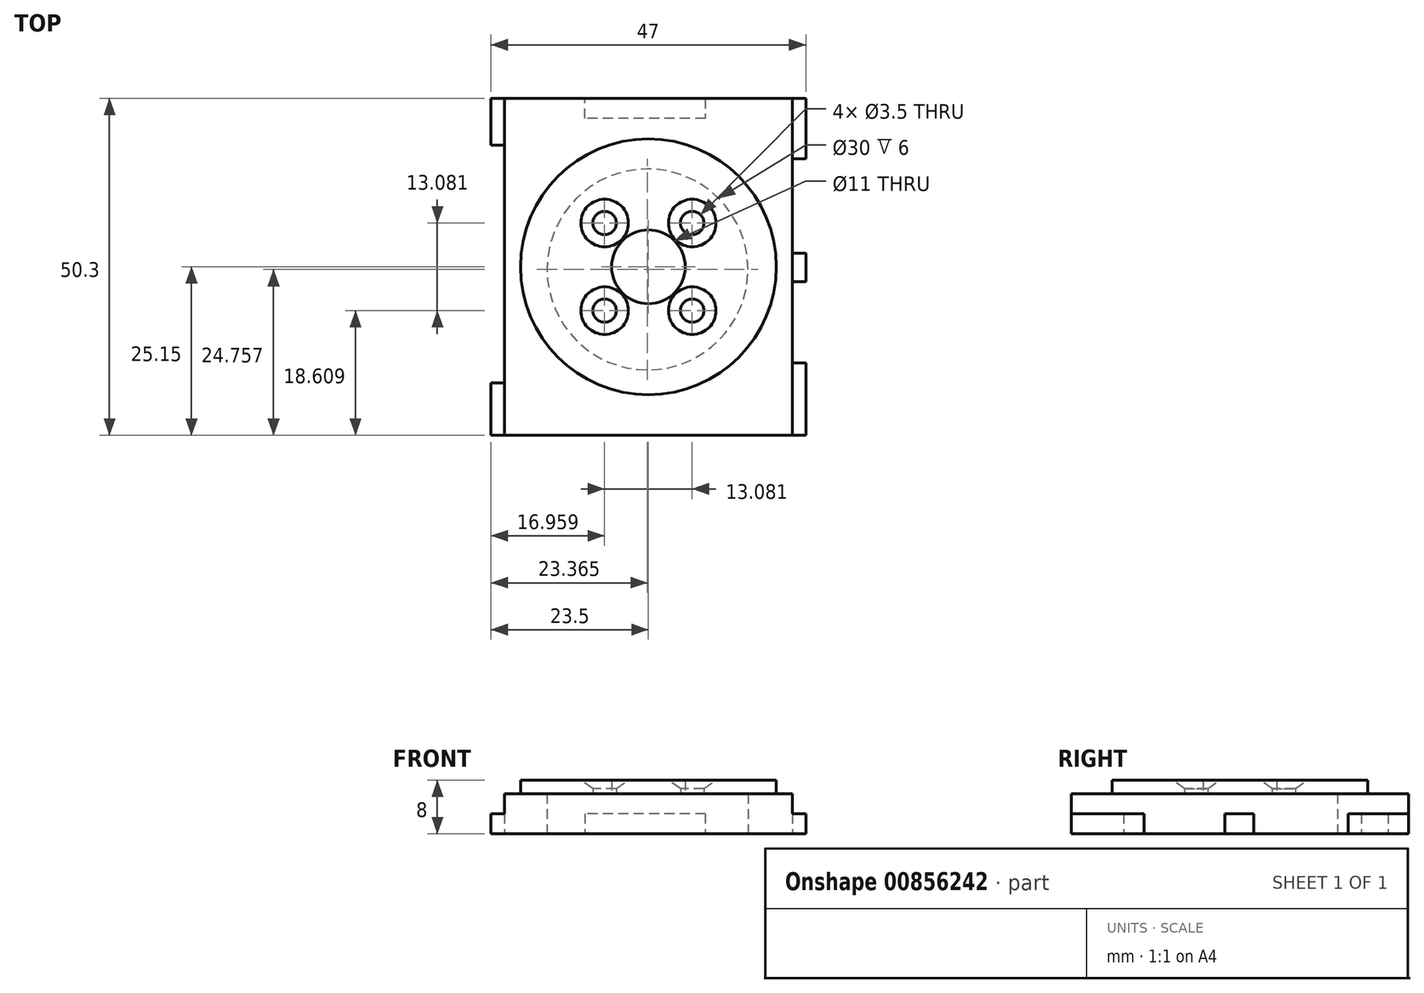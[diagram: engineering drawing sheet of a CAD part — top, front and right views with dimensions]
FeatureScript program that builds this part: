
annotation { "Feature Type Name" : "Feature", "Feature Type Description" : "" }
export const myFeature = defineFeature(function(context is Context, id is Id, definition is map)
    precondition{}
    {
        {
            var Q0;
            Q0=qCreatedBy(makeId("Top.planeOp"),FACE);
            var sketch = newSketch(context, id + "F0", { "sketchPlane" : qUnion([Q0])});
            skLineSegment(sketch, "E0.bottom", {"start": v(-23.5, 25.15) * mm, "end": v(-9.5, 25.15) * mm});
            skLineSegment(sketch, "E0.top", {"start": v(-23.5, -25.15) * mm, "end": v(23.5, -25.15) * mm});
            skLineSegment(sketch, "E0.right", {"start": v(23.5, 25.15) * mm, "end": v(23.5, 16.15) * mm});
            skPoint(sketch, "E0.middle", {"position": v(0, 0) * mm});
            skCircle(sketch, "E1", {"center": v(23.5, 25.15) * mm, "radius": 9 * mm, "construction": true});
            skLineSegment(sketch, "E2", {"start": v(23.5, 16.15) * mm, "end": v(21.5, 16.15) * mm});
            skLineSegment(sketch, "E3", {"start": v(21.5, 16.15) * mm, "end": v(21.5, 2.15) * mm});
            skLineSegment(sketch, "E4", {"start": v(21.5, 2.15) * mm, "end": v(23.5, 2.15) * mm});
            skLineSegment(sketch, "E5", {"start": v(23.5, 2.15) * mm, "end": v(23.5, -2.35) * mm});
            skLineSegment(sketch, "E6", {"start": v(23.5, -2.35) * mm, "end": v(21.5, -2.35) * mm});
            skLineSegment(sketch, "E7", {"start": v(21.5, -2.35) * mm, "end": v(21.5, -14.35) * mm});
            skLineSegment(sketch, "E8", {"start": v(21.5, -14.35) * mm, "end": v(23.5, -14.35) * mm});
            skLineSegment(sketch, "E9", {"start": v(23.5, -14.35) * mm, "end": v(23.5, -25.15) * mm});
            skCircle(sketch, "E10", {"center": v(23.5, -25.15) * mm, "radius": 13 * mm, "construction": true});
            skCircle(sketch, "E11", {"center": v(-23.5, -25.15) * mm, "radius": 13 * mm, "construction": true});
            skCircle(sketch, "E12", {"center": v(23.5, 25.15) * mm, "radius": 34.8 * mm, "construction": true});
            skCircle(sketch, "E13", {"center": v(-23.5, 25.15) * mm, "radius": 2 * mm, "construction": true});
            skCircle(sketch, "E14", {"center": v(-21.5, 25.15) * mm, "radius": 33.3 * mm, "construction": true});
            skCircle(sketch, "E15", {"center": v(-0.13, -0.4) * mm, "radius": 5.5 * mm});
            skLineSegment(sketch, "E16", {"start": v(-23.5, 25.15) * mm, "end": v(-23.5, 18.15) * mm});
            skLineSegment(sketch, "E17", {"start": v(-23.5, 18.15) * mm, "end": v(-21.5, 18.15) * mm});
            skLineSegment(sketch, "E18", {"start": v(-23.5, -25.15) * mm, "end": v(-23.5, -12.15) * mm});
            skLineSegment(sketch, "E19", {"start": v(-23.5, -25.15) * mm, "end": v(-23.5, -17.35) * mm});
            skLineSegment(sketch, "E20", {"start": v(-23.5, -17.35) * mm, "end": v(-21.5, -17.35) * mm});
            skLineSegment(sketch, "E21", {"start": v(-21.5, -17.35) * mm, "end": v(-21.5, 18.15) * mm});
            skCircle(sketch, "E22", {"center": v(-0.13, -0.4) * mm, "radius": 15 * mm});
            skLineSegment(sketch, "E23", {"start": v(23.5, 25.15) * mm, "end": v(8.5, 25.15) * mm});
            skLineSegment(sketch, "E24", {"start": v(8.5, 25.15) * mm, "end": v(8.5, 22.15) * mm});
            skLineSegment(sketch, "E25", {"start": v(8.5, 22.15) * mm, "end": v(-9.5, 22.15) * mm});
            skLineSegment(sketch, "E26", {"start": v(-9.5, 22.15) * mm, "end": v(-9.5, 25.15) * mm});
            skLineSegment(sketch, "E27.trimOffspring", {"start": v(8.5, 25.15) * mm, "end": v(23.5, 25.15) * mm});
            skSolve(sketch);
        }
        {
            var Q0;
            Q0=makeQuery(id+"F0.imprint","IMPRINT",FACE,{"disambiguationData":[TD([[makeQuery(id+"F0.imprint","IMPRINT",EDGE,{"derivedFrom":sQuery(id+"F0.wireOp",EDGE,"E0.bottom")}),-1.0]])]});
            extrude(context, id + "F1", {"entities" : qUnion([Q0]), "depth" : 3 * mm, "offsetDistance" : 25 * mm});
        }
        {
            var Q0;
            Q0=makeQuery(id+"F1.opExtrude","CAP_FACE",FACE,{"disambiguationData":[OSD([sQuery(id+"F0.wireOp",EDGE,"E0.bottom"),sQuery(id+"F0.wireOp",EDGE,"E0.top"),sQuery(id+"F0.wireOp",EDGE,"E0.right"),sQuery(id+"F0.wireOp",EDGE,"E2"),sQuery(id+"F0.wireOp",EDGE,"E3"),sQuery(id+"F0.wireOp",EDGE,"E4"),sQuery(id+"F0.wireOp",EDGE,"E6"),sQuery(id+"F0.wireOp",EDGE,"E7"),sQuery(id+"F0.wireOp",EDGE,"E8"),sQuery(id+"F0.wireOp",EDGE,"E5"),sQuery(id+"F0.wireOp",EDGE,"E9"),sQuery(id+"F0.wireOp",EDGE,"E16"),sQuery(id+"F0.wireOp",EDGE,"E17"),sQuery(id+"F0.wireOp",EDGE,"E19"),sQuery(id+"F0.wireOp",EDGE,"E20"),sQuery(id+"F0.wireOp",EDGE,"E21"),sQuery(id+"F0.wireOp",EDGE,"E22"),sQuery(id+"F0.wireOp",EDGE,"E24"),sQuery(id+"F0.wireOp",EDGE,"E25"),sQuery(id+"F0.wireOp",EDGE,"E26"),sQuery(id+"F0.wireOp",EDGE,"E27.trimOffspring")])],"isStart":false});
            var sketch = newSketch(context, id + "F2", { "sketchPlane" : qUnion([Q0])});
            skLineSegment(sketch, "E28", {"start": v(-21.5, 18.15) * mm, "end": v(-21.5, 25.15) * mm});
            skLineSegment(sketch, "E29", {"start": v(21.5, 16.15) * mm, "end": v(21.5, 25.15) * mm, "construction": true});
            skLineSegment(sketch, "E30", {"start": v(21.5, 25.15) * mm, "end": v(21.5, -25.15) * mm});
            skLineSegment(sketch, "E31", {"start": v(-21.5, -17.35) * mm, "end": v(-21.5, -25.15) * mm});
            skLineSegment(sketch, "E32", {"start": v(-9.5, 25.15) * mm, "end": v(8.5, 25.15) * mm});
            skSolve(sketch);
        }
        {
            var Q0;
            {var subQ8=sQuery(id+"F2.wireOp",EDGE,"E28");Q0=makeQuery(id+"F2.imprint","IMPRINT",FACE,{"disambiguationData":[TD([[makeQuery(id+"F2.imprint","IMPRINT",EDGE,{"derivedFrom":subQ8}),-1.0]])]});}
            var Q1;
            Q1=makeQuery(id+"F2.imprint","IMPRINT",FACE,{"disambiguationData":[TD([[makeQuery(id+"F2.imprint","IMPRINT",EDGE,{"derivedFrom":sQuery(id+"F2.wireOp",EDGE,"E32")}),-1.0]])]});
            extrude(context, id + "F3", {"entities" : qUnion([Q0, Q1]), "operationType" : NewBodyOperationType.ADD, "depth" : 3 * mm, "offsetDistance" : 25 * mm});
        }
        {
            var Q0;
            Q0=makeQuery(id+"F3.opExtrude","CAP_FACE",FACE,{"disambiguationData":[OSD([sQuery(id+"F0.wireOp",EDGE,"E0.bottom"),sQuery(id+"F0.wireOp",EDGE,"E0.top"),sQuery(id+"F0.wireOp",EDGE,"E21"),sQuery(id+"F0.wireOp",EDGE,"E22"),sQuery(id+"F0.wireOp",EDGE,"E27.trimOffspring"),sQuery(id+"F2.wireOp",EDGE,"E28"),sQuery(id+"F2.wireOp",EDGE,"E30"),sQuery(id+"F2.wireOp",EDGE,"E31"),sQuery(id+"F2.wireOp",EDGE,"E32")])],"isStart":false});
            var sketch = newSketch(context, id + "F4", { "sketchPlane" : qUnion([Q0])});
            skCircle(sketch, "E33", {"center": v(0, 0) * mm, "radius": 5.5 * mm});
            skLineSegment(sketch, "E34", {"start": v(0, 0) * mm, "end": v(13.5, 13.5) * mm, "construction": true});
            skLineSegment(sketch, "E35", {"start": v(0, 0) * mm, "end": v(16.52, 0) * mm, "construction": true});
            skLineSegment(sketch, "E36", {"start": v(0, 0) * mm, "end": v(0, 17.7) * mm, "construction": true});
            skLineSegment(sketch, "E37.MirrorCS", {"start": v(0, 0) * mm, "end": v(-13.5, 13.5) * mm, "construction": true});
            skLineSegment(sketch, "E38.MirrorCS", {"start": v(0, 0) * mm, "end": v(13.5, -13.5) * mm, "construction": true});
            skLineSegment(sketch, "E39.MirrorCS", {"start": v(0, 0) * mm, "end": v(-13.5, -13.5) * mm, "construction": true});
            skCircle(sketch, "E40", {"center": v(0, 0) * mm, "radius": 9.25 * mm, "construction": true});
            skCircle(sketch, "E41", {"center": v(6.54, 6.54) * mm, "radius": 1.75 * mm});
            skCircle(sketch, "E42.MirrorC", {"center": v(-6.54, 6.54) * mm, "radius": 1.75 * mm});
            skCircle(sketch, "E43.MirrorC", {"center": v(6.54, -6.54) * mm, "radius": 1.75 * mm});
            skCircle(sketch, "E44.MirrorC", {"center": v(-6.54, -6.54) * mm, "radius": 1.75 * mm});
            skCircle(sketch, "E45", {"center": v(0, 0) * mm, "radius": 19.1 * mm});
            skSolve(sketch);
        }
        {
            var Q0;
            Q0=makeQuery(id+"F4.imprint","IMPRINT",FACE,{"disambiguationData":[TD([[makeQuery(id+"F4.imprint","IMPRINT",EDGE,{"derivedFrom":sQuery(id+"F4.wireOp",EDGE,"E45")}),1.0]])]});
            var Q1;
            Q1=makeQuery(id+"F4.imprint","IMPRINT",FACE,{"disambiguationData":[TD([[makeQuery(id+"F4.imprint","IMPRINT",EDGE,{"derivedFrom":sQuery(id+"F4.wireOp",EDGE,"E33")}),-1.0]])]});
            extrude(context, id + "F5", {"entities" : qUnion([Q0, Q1]), "operationType" : NewBodyOperationType.ADD, "depth" : 2 * mm, "offsetDistance" : 25 * mm});
        }
        {
            var Q0;
            Q0=makeQuery(id+"F5.opExtrude","CAP_EDGE",EDGE,{"disambiguationData":[OSD([sQuery(id+"F4.wireOp",EDGE,"E42.MirrorC")])],"isStart":false});
            var Q1;
            Q1=makeQuery(id+"F5.opExtrude","CAP_EDGE",EDGE,{"disambiguationData":[OSD([sQuery(id+"F4.wireOp",EDGE,"E41")])],"isStart":false});
            var Q2;
            Q2=makeQuery(id+"F5.opExtrude","CAP_EDGE",EDGE,{"disambiguationData":[OSD([sQuery(id+"F4.wireOp",EDGE,"E43.MirrorC")])],"isStart":false});
            var Q3;
            Q3=makeQuery(id+"F5.opExtrude","CAP_EDGE",EDGE,{"disambiguationData":[OSD([sQuery(id+"F4.wireOp",EDGE,"E44.MirrorC")])],"isStart":false});
            chamfer(context, id + "F6", {"entities" : qUnion([Q0, Q1, Q2, Q3]), "chamferType" : ChamferType.TWO_OFFSETS, "width1" : 1.25 * mm, "oppositeDirection" : false, "width2" : 1.8 * mm, "tangentPropagation" : true});
        }
        {
            var Q0;
            {var subQ0=sQuery(id+"F0.wireOp",EDGE,"E7");var subQ1=sQuery(id+"F0.wireOp",EDGE,"E6");var subQ2=sQuery(id+"F0.wireOp",EDGE,"E4");var subQ3=sQuery(id+"F0.wireOp",EDGE,"E3");var subQ4=sQuery(id+"F0.wireOp",EDGE,"E5");Q0=makeQuery(id+"F3.boolean.opBoolean","SPLIT",FACE,{"disambiguationData":[TD([makeQuery(id+"F1.opExtrude","SWEPT_FACE",FACE,{"disambiguationData":[OSD([subQ2])]})])],"derivedFrom":makeQuery(id+"F1.opExtrude","CAP_FACE",FACE,{"disambiguationData":[OSD([sQuery(id+"F0.wireOp",EDGE,"E0.bottom"),sQuery(id+"F0.wireOp",EDGE,"E0.top"),sQuery(id+"F0.wireOp",EDGE,"E0.right"),sQuery(id+"F0.wireOp",EDGE,"E2"),subQ3,subQ2,subQ1,subQ0,sQuery(id+"F0.wireOp",EDGE,"E8"),subQ4,sQuery(id+"F0.wireOp",EDGE,"E9"),sQuery(id+"F0.wireOp",EDGE,"E16"),sQuery(id+"F0.wireOp",EDGE,"E17"),sQuery(id+"F0.wireOp",EDGE,"E19"),sQuery(id+"F0.wireOp",EDGE,"E20"),sQuery(id+"F0.wireOp",EDGE,"E21"),sQuery(id+"F0.wireOp",EDGE,"E22"),sQuery(id+"F0.wireOp",EDGE,"E24"),sQuery(id+"F0.wireOp",EDGE,"E25"),sQuery(id+"F0.wireOp",EDGE,"E26"),sQuery(id+"F0.wireOp",EDGE,"E27.trimOffspring")])],"isStart":false})});}
            var sketch = newSketch(context, id + "F7", { "sketchPlane" : qUnion([Q0])});
            skLineSegment(sketch, "E46.bottom", {"start": v(21.5, 2.15) * mm, "end": v(23.5, 2.15) * mm});
            skLineSegment(sketch, "E46.top", {"start": v(21.5, 2.05) * mm, "end": v(23.5, 2.05) * mm});
            skLineSegment(sketch, "E46.left", {"start": v(21.5, 2.15) * mm, "end": v(21.5, 2.05) * mm});
            skLineSegment(sketch, "E46.right", {"start": v(23.5, 2.15) * mm, "end": v(23.5, 2.05) * mm});
            skLineSegment(sketch, "E47.bottom", {"start": v(23.5, -2.35) * mm, "end": v(21.5, -2.35) * mm});
            skLineSegment(sketch, "E47.top", {"start": v(23.5, -2.25) * mm, "end": v(21.5, -2.25) * mm});
            skLineSegment(sketch, "E47.left", {"start": v(23.5, -2.35) * mm, "end": v(23.5, -2.25) * mm});
            skLineSegment(sketch, "E47.right", {"start": v(21.5, -2.35) * mm, "end": v(21.5, -2.25) * mm});
            skSolve(sketch);
        }
        {
            var Q0;
            Q0=makeQuery(id+"F7.imprint","IMPRINT",FACE,{"disambiguationData":[TD([[makeQuery(id+"F7.imprint","IMPRINT",EDGE,{"derivedFrom":sQuery(id+"F7.wireOp",EDGE,"E46.bottom")}),-1.0]])]});
            var Q1;
            Q1=makeQuery(id+"F7.imprint","IMPRINT",FACE,{"disambiguationData":[TD([[makeQuery(id+"F7.imprint","IMPRINT",EDGE,{"derivedFrom":sQuery(id+"F7.wireOp",EDGE,"E47.bottom")}),-1.0]])]});
            extrude(context, id + "F8", {"entities" : qUnion([Q0, Q1]), "operationType" : NewBodyOperationType.REMOVE, "endBound" : BoundingType.THROUGH_ALL, "oppositeDirection" : true, "depth" : 25 * mm, "offsetDistance" : 25 * mm});
        }
    });
